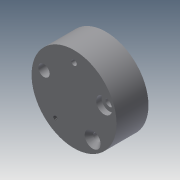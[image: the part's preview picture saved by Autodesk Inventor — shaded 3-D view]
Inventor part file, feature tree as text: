
AUTODESK INVENTOR PART (.ipt)
format: ipt  version: 2015 (Build 190159000, 159)  size: 102,912 bytes
history: native  units: in
note: dims shown in document units (in); Inventor stores cm internally (conversion verified against a paired STEP export)
features: hole x5, sketch x2, extrude x1, projected_geometry x1
ambient origin geometry x8: Origin, YZ Plane, XZ Plane, XY Plane, X Axis, Y Axis, Z Axis, Center Point
bodies: Solid1 (feature_tree)
feature tree (9):
  extrude  "Extrusion1"  Depth=1.5in TaperAngle=0.0deg
  sketch  "Sketch2"  dims[d3=1.9685in d5=360.0deg d7=0.25in d8=0.75in d9=0.375in d10=0.25in d11=0.5635in d12=1.0in d13=0.8108in d14=0.375in d15=0.75in d16=0.75in d17=0.25in d18=0.5635in d19=1.0in d20=0.8108in d21=0.375in d22=0.75in d23=0.75in d24=0.25in d25=0.5635in d26=1.0in d27=0.8108in d28=0.196in d29=0.5in d30=0.75in d31=0.25in d32=0.5635in d33=0.75in d34=0.8108in d35=0.531in d36=0.5in d37=1.125in d38=0.364in d39=0.5635in d40=0.75in d41=0.8108in]
  hole  "Hole1"  [1 undecoded]
  hole  "Hole2"  [1 undecoded]
  hole  "Hole3"  [1 undecoded]
  hole  "Hole4"  [1 undecoded]
  hole  "Hole5"  [1 undecoded]
  sketch  "Sketch1"  dims[d0=4.0in d1=1.5in d2=0.0in]
  projected_geometry  "Projected Loop1"
note: 5 required parameter values undecoded (feature->parameter linkage not recoverable at this tier; creation-order binding heuristic only, values carry confidence <= 0.55)
